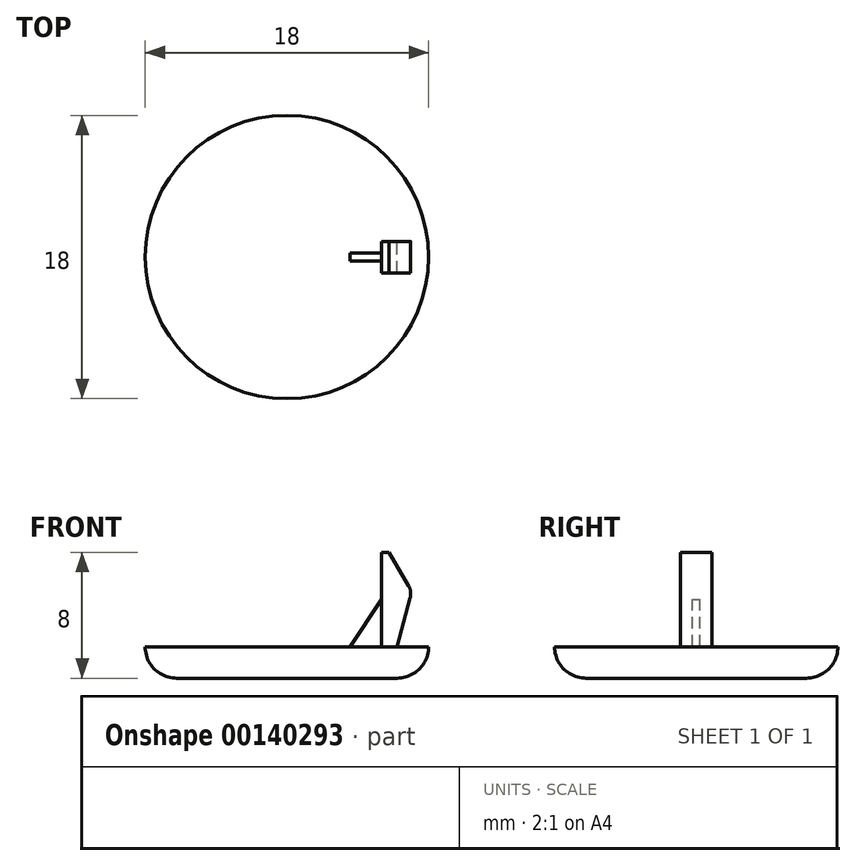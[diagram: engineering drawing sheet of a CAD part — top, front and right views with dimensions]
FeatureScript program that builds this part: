
annotation { "Feature Type Name" : "Feature", "Feature Type Description" : "" }
export const myFeature = defineFeature(function(context is Context, id is Id, definition is map)
    precondition{}
    {
        {
            var Q0;
            Q0=qCreatedBy(makeId("Front.planeOp"),FACE);
            var sketch = newSketch(context, id + "F0", { "sketchPlane" : qUnion([Q0])});
            skLineSegment(sketch, "E0", {"start": v(0, 0) * mm, "end": v(4, 0) * mm, "construction": true});
            skLineSegment(sketch, "E1", {"start": v(4, 0) * mm, "end": v(6, 0) * mm});
            skLineSegment(sketch, "E2", {"start": v(6, 0) * mm, "end": v(7, 0) * mm});
            skLineSegment(sketch, "E3", {"start": v(6, 0) * mm, "end": v(6, 6) * mm});
            skLineSegment(sketch, "E4", {"start": v(6, 0) * mm, "end": v(6, 3) * mm});
            skLineSegment(sketch, "E5", {"start": v(4, 0) * mm, "end": v(6, 3) * mm});
            skLineSegment(sketch, "E6", {"start": v(6, 6) * mm, "end": v(6.5, 6) * mm});
            skLineSegment(sketch, "E7", {"start": v(6.5, 6) * mm, "end": v(7.73, 3.87) * mm});
            skLineSegment(sketch, "E8", {"start": v(7, 0) * mm, "end": v(7.83, 3.1) * mm});
            skArc(sketch, "E9", {"start": v(7.83, 3.1) * mm, "mid": v(7.86, 3.5) * mm, "end": v(7.73, 3.87) * mm});
            skSolve(sketch);
        }
        {
            var Q0;
            Q0=makeQuery(id+"F0.imprint","IMPRINT",FACE,{"disambiguationData":[TD([[makeQuery(id+"F0.imprint","IMPRINT",EDGE,{"derivedFrom":sQuery(id+"F0.wireOp",EDGE,"E2")}),1.0]])]});
            extrude(context, id + "F1", {"entities" : qUnion([Q0]), "endBound" : BoundingType.SYMMETRIC, "depth" : 2 * mm});
        }
        {
            var Q0;
            Q0=makeQuery(id+"F0.imprint","IMPRINT",FACE,{"disambiguationData":[TD([[makeQuery(id+"F0.imprint","IMPRINT",EDGE,{"derivedFrom":sQuery(id+"F0.wireOp",EDGE,"E1")}),1.0]])]});
            extrude(context, id + "F2", {"entities" : qUnion([Q0]), "operationType" : NewBodyOperationType.ADD, "endBound" : BoundingType.SYMMETRIC, "depth" : 0.5 * mm});
        }
        {
            var Q0;
            Q0=qCreatedBy(makeId("Top.planeOp"),FACE);
            var sketch = newSketch(context, id + "F3", { "sketchPlane" : qUnion([Q0])});
            skCircle(sketch, "E10", {"center": v(0, 0) * mm, "radius": 9 * mm});
            skSolve(sketch);
        }
        {
            var Q0;
            Q0=makeQuery(id+"F3.imprint","IMPRINT",FACE,{"disambiguationData":[TD([[makeQuery(id+"F3.imprint","IMPRINT",EDGE,{"derivedFrom":sQuery(id+"F3.wireOp",EDGE,"E10")}),1.0]])]});
            extrude(context, id + "F4", {"entities" : qUnion([Q0]), "operationType" : NewBodyOperationType.ADD, "oppositeDirection" : true, "depth" : 2 * mm});
        }
        {
            var Q0;
            Q0=makeQuery(id+"F4.opExtrude","CAP_EDGE",EDGE,{"disambiguationData":[OSD([sQuery(id+"F3.wireOp",EDGE,"E10")])],"isStart":false});
            fillet(context, id + "F5", {"entities" : qUnion([Q0]), "radius" : 2 * mm, "tangentPropagation" : true, "allowEdgeOverflow" : false});
        }
    });
